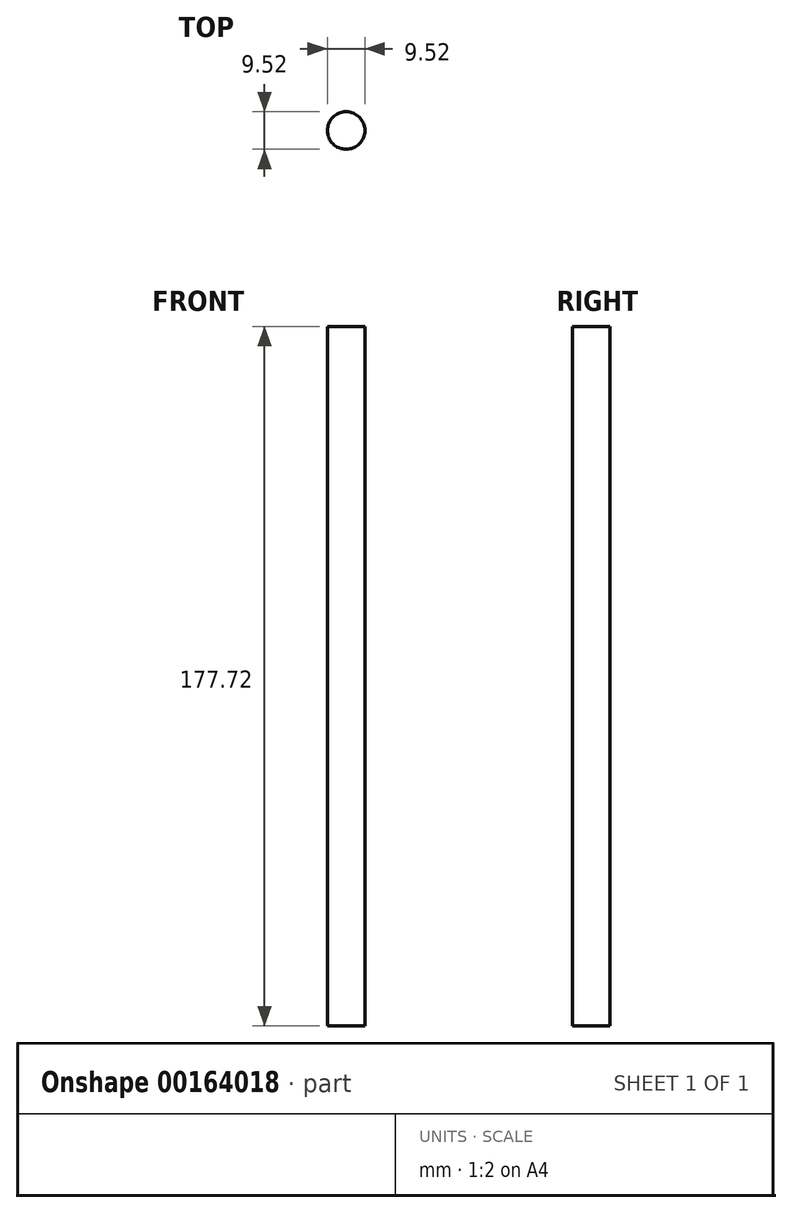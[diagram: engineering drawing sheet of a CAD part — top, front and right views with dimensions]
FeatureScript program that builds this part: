
annotation { "Feature Type Name" : "Feature", "Feature Type Description" : "" }
export const myFeature = defineFeature(function(context is Context, id is Id, definition is map)
    precondition{}
    {
        {
            var Q0;
            Q0=qCreatedBy(makeId("Top.planeOp"),FACE);
            var sketch = newSketch(context, id + "F0", { "sketchPlane" : qUnion([Q0])});
            skCircle(sketch, "E0", {"center": v(0, 0) * mm, "radius": 4.76 * mm});
            skSolve(sketch);
        }
        {
            var Q0;
            Q0=makeQuery(id+"F0.imprint","IMPRINT",FACE,{"disambiguationData":[TD([[makeQuery(id+"F0.imprint","IMPRINT",EDGE,{"derivedFrom":sQuery(id+"F0.wireOp",EDGE,"E0")}),1.0]])]});
            extrude(context, id + "F1", {"entities" : qUnion([Q0]), "depth" : 177.72 * mm});
        }
    });
